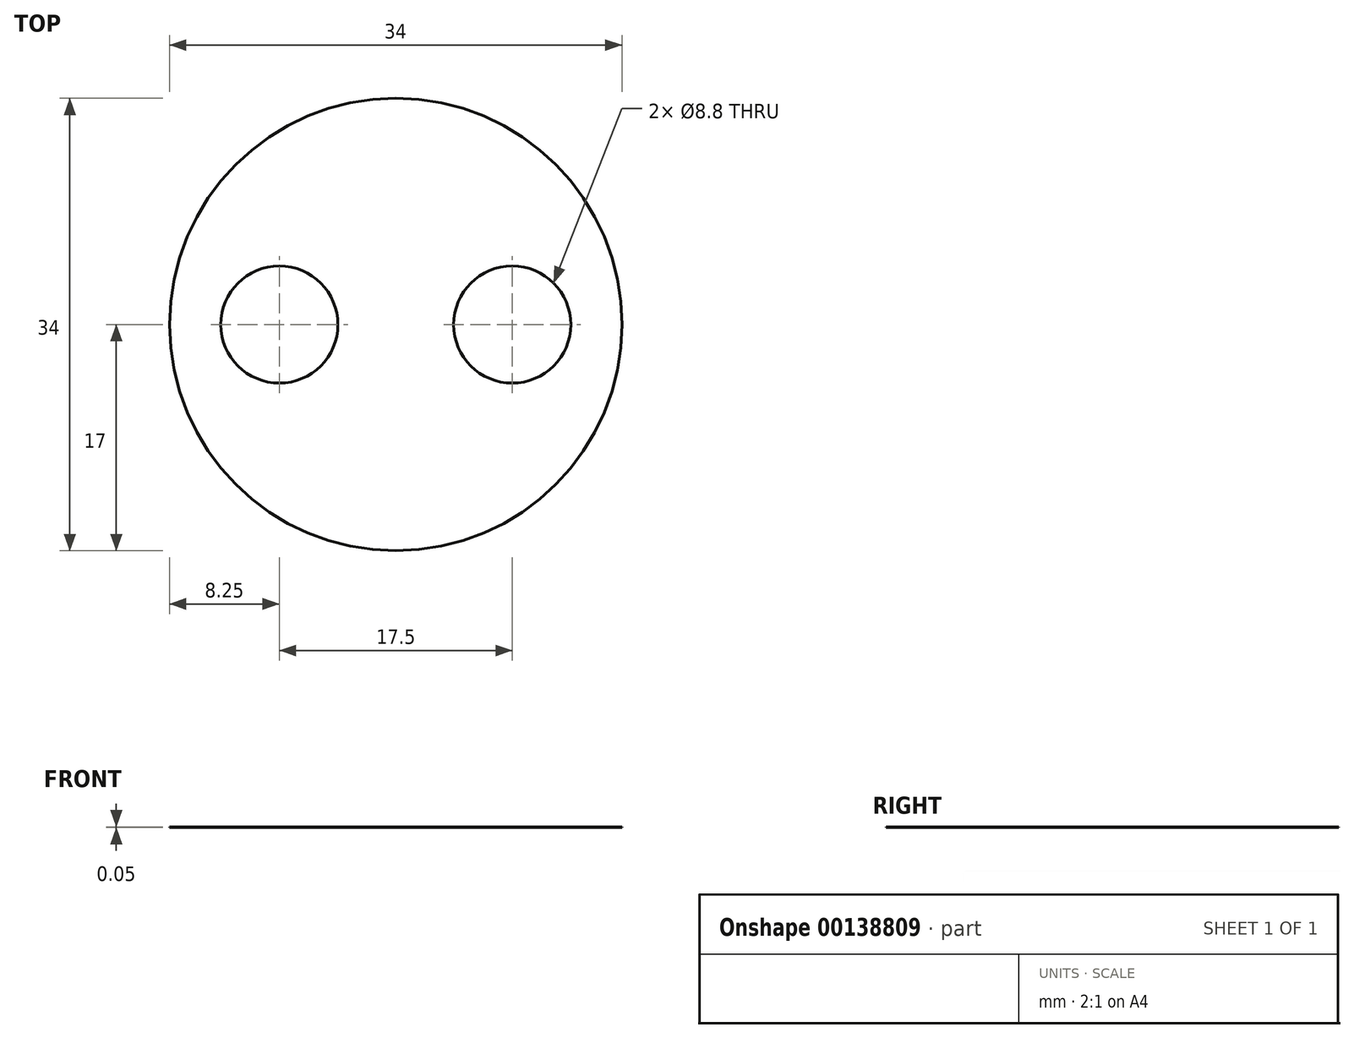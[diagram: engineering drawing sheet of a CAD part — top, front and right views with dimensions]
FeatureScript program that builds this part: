
annotation { "Feature Type Name" : "Feature", "Feature Type Description" : "" }
export const myFeature = defineFeature(function(context is Context, id is Id, definition is map)
    precondition{}
    {
        {
            var Q0;
            Q0=qCreatedBy(makeId("Top.planeOp"),FACE);
            var sketch = newSketch(context, id + "F0", { "sketchPlane" : qUnion([Q0])});
            skCircle(sketch, "E0", {"center": v(0, 0) * mm, "radius": 17 * mm});
            skCircle(sketch, "E1", {"center": v(-8.75, 0) * mm, "radius": 4.4 * mm});
            skCircle(sketch, "E2.MirrorC", {"center": v(8.75, 0) * mm, "radius": 4.4 * mm});
            skSolve(sketch);
        }
        {
            var Q0;
            Q0 = qSketchRegion(id + "F0", true);
            extrude(context, id + "F1", {"entities" : qUnion([Q0]), "depth" : 0.05 * mm});
        }
    });
